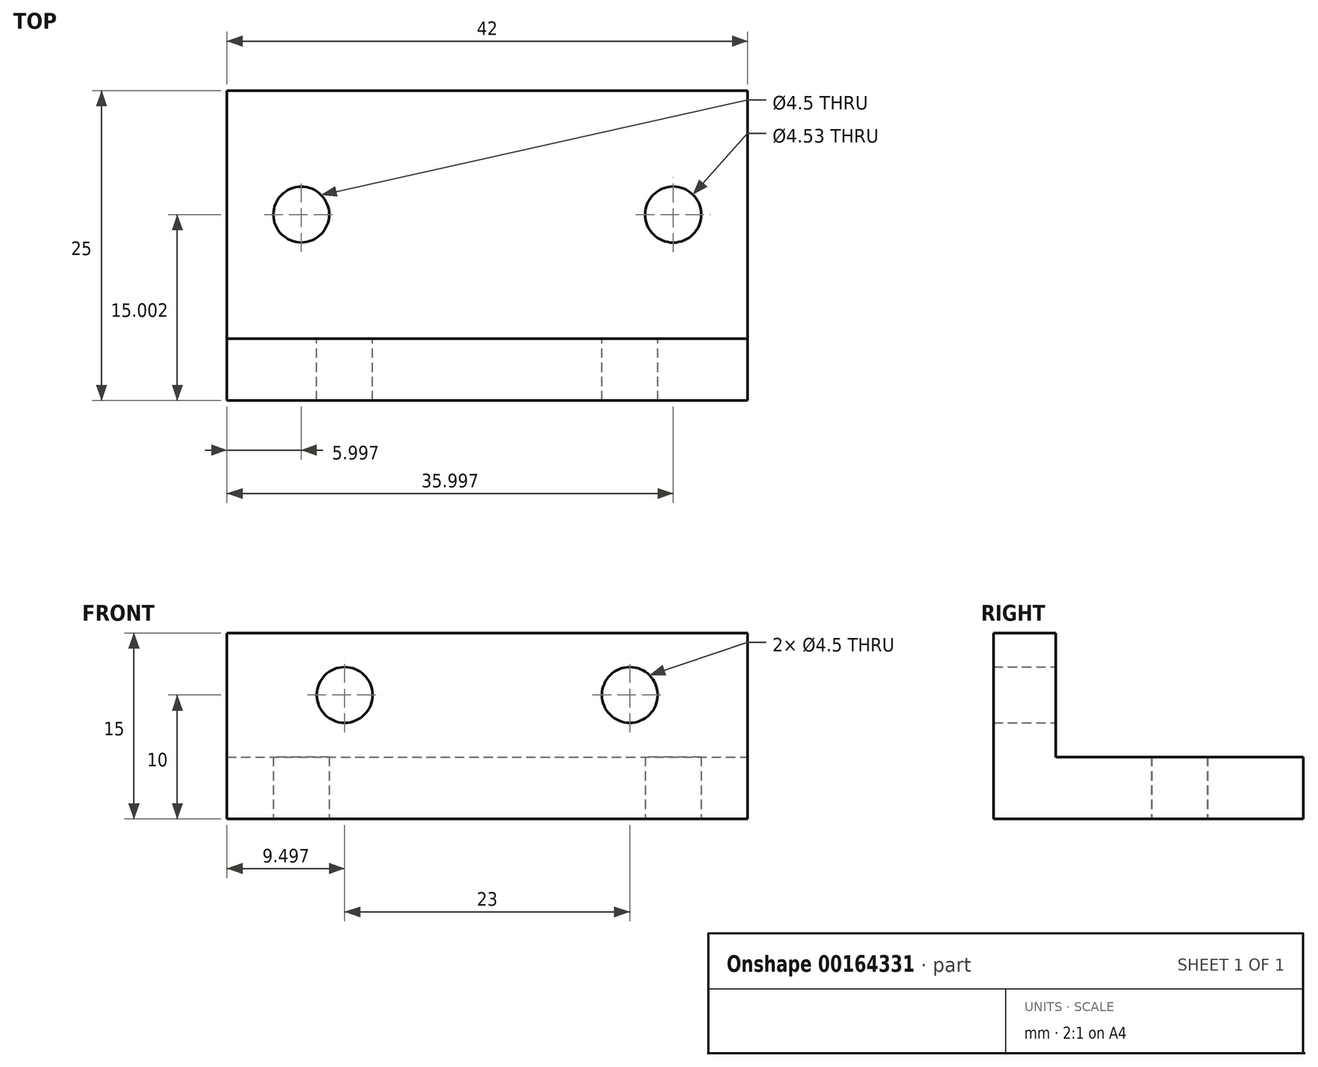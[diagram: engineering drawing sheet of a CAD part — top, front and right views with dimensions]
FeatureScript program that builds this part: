
annotation { "Feature Type Name" : "Feature", "Feature Type Description" : "" }
export const myFeature = defineFeature(function(context is Context, id is Id, definition is map)
    precondition{}
    {
        {
            var Q0;
            Q0=qCreatedBy(makeId("Top.planeOp"),FACE);
            var sketch = newSketch(context, id + "F0", { "sketchPlane" : qUnion([Q0])});
            skLineSegment(sketch, "E0.bottom", {"start": v(-19.36, 10.26) * mm, "end": v(22.64, 10.26) * mm});
            skLineSegment(sketch, "E0.top", {"start": v(-19.36, -14.74) * mm, "end": v(22.64, -14.74) * mm});
            skLineSegment(sketch, "E0.left", {"start": v(-19.36, 10.26) * mm, "end": v(-19.36, -14.74) * mm});
            skLineSegment(sketch, "E0.right", {"start": v(22.64, 10.26) * mm, "end": v(22.64, -14.74) * mm});
            skLineSegment(sketch, "E1", {"start": v(-19.36, -9.74) * mm, "end": v(22.64, -9.74) * mm});
            skCircle(sketch, "E2", {"center": v(-13.36, 0.26) * mm, "radius": 2.25 * mm});
            skCircle(sketch, "E3", {"center": v(16.64, 0.26) * mm, "radius": 2.26 * mm});
            skSolve(sketch);
        }
        {
            var Q0;
            Q0 = qSketchRegion(id + "F0", true);
            extrude(context, id + "F1", {"entities" : qUnion([Q0]), "depth" : 5 * mm});
        }
        {
            var Q0;
            {var subQ0=sQuery(id+"F0.wireOp",EDGE,"E0.top");Q0=makeQuery(id+"F0.imprint","IMPRINT",FACE,{"disambiguationData":[TD([[makeQuery(id+"F0.imprint","IMPRINT",EDGE,{"derivedFrom":subQ0}),1.0]])]});}
            extrude(context, id + "F2", {"entities" : qUnion([Q0]), "operationType" : NewBodyOperationType.ADD, "depth" : 15 * mm});
        }
        {
            var Q0;
            Q0=makeQuery(id+"F2.opExtrude","SWEPT_FACE",FACE,{"disambiguationData":[OSD([sQuery(id+"F0.wireOp",EDGE,"E1")])]});
            var sketch = newSketch(context, id + "F3", { "sketchPlane" : qUnion([Q0])});
            skCircle(sketch, "E4", {"center": v(-13.14, 10) * mm, "radius": 2.25 * mm});
            skPoint(sketch, "E4.centerSnap0", {"position": v(-22.64, 10) * mm});
            skCircle(sketch, "E5", {"center": v(9.86, 10) * mm, "radius": 2.25 * mm});
            skSolve(sketch);
        }
        {
            var Q0;
            Q0 = qSketchRegion(id + "F3", true);
            extrude(context, id + "F4", {"entities" : qUnion([Q0]), "operationType" : NewBodyOperationType.REMOVE, "oppositeDirection" : true, "depth" : 10 * mm});
        }
    });
